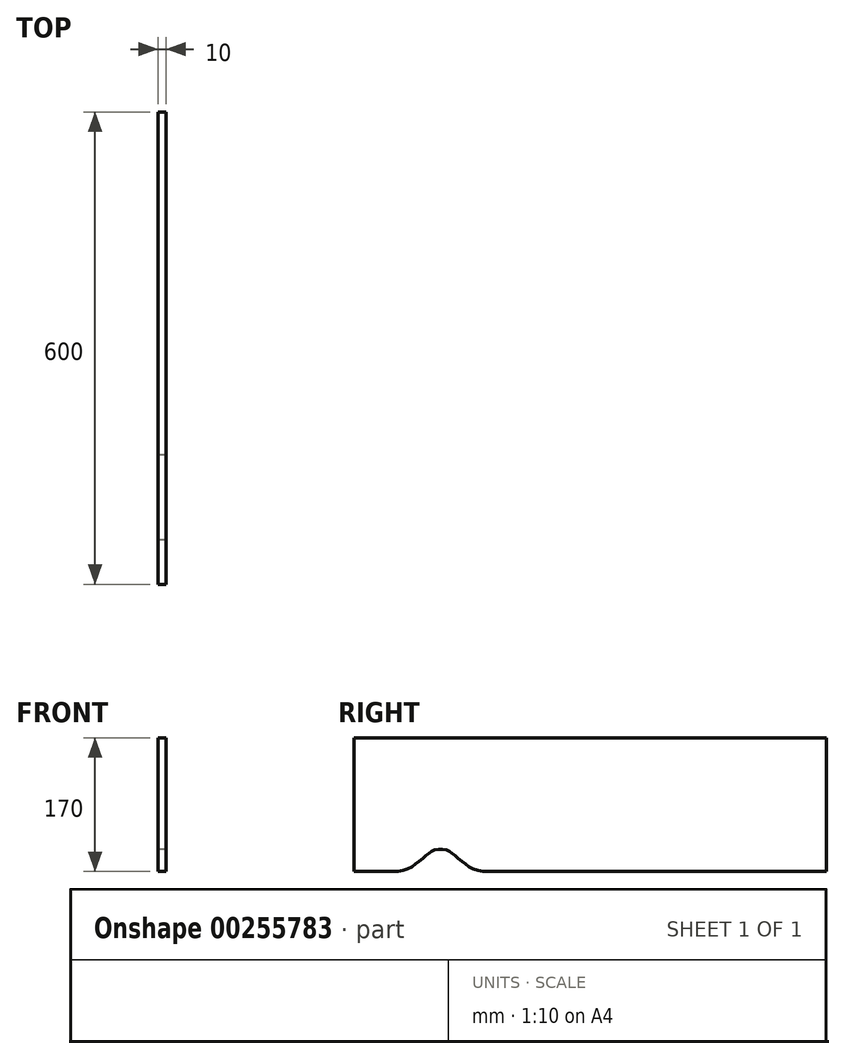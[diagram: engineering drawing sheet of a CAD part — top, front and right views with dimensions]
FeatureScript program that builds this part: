
annotation { "Feature Type Name" : "Feature", "Feature Type Description" : "" }
export const myFeature = defineFeature(function(context is Context, id is Id, definition is map)
    precondition{}
    {
        {
            var Q0;
            Q0=qCreatedBy(makeId("Right.planeOp"),FACE);
            var sketch = newSketch(context, id + "F0", { "sketchPlane" : qUnion([Q0])});
            skLineSegment(sketch, "E0.bottom", {"start": v(0, 0) * mm, "end": v(600, 0) * mm});
            skLineSegment(sketch, "E0.top", {"start": v(0, 170) * mm, "end": v(600, 170) * mm});
            skLineSegment(sketch, "E0.left", {"start": v(0, 0) * mm, "end": v(0, 170) * mm});
            skLineSegment(sketch, "E0.right", {"start": v(600, 0) * mm, "end": v(600, 170) * mm});
            skLineSegment(sketch, "E1", {"start": v(0, 0) * mm, "end": v(56, 0) * mm});
            skFitSpline(sketch, "E2", {"points": [v(56, 0) * mm, v(70, 4) * mm, v(80, 11) * mm, v(90, 19) * mm, v(96, 24) * mm, v(101, 27) * mm, v(110, 28) * mm, v(119, 27) * mm, v(124, 24) * mm, v(130, 19) * mm, v(140, 11) * mm, v(150, 4) * mm, v(164, 0) * mm], "startDerivative": vector(149.1, 30.84) * mm, "endDerivative": vector(149.1, -30.84) * mm});
            skSolve(sketch);
        }
        {
            var Q0;
            Q0=makeQuery(id+"F0.imprint","IMPRINT",FACE,{"disambiguationData":[TD([[makeQuery(id+"F0.imprint","IMPRINT",EDGE,{"derivedFrom":sQuery(id+"F0.wireOp",EDGE,"E0.top")}),-1.0]])]});
            extrude(context, id + "F1", {"entities" : qUnion([Q0]), "depth" : 10 * mm});
        }
    });
